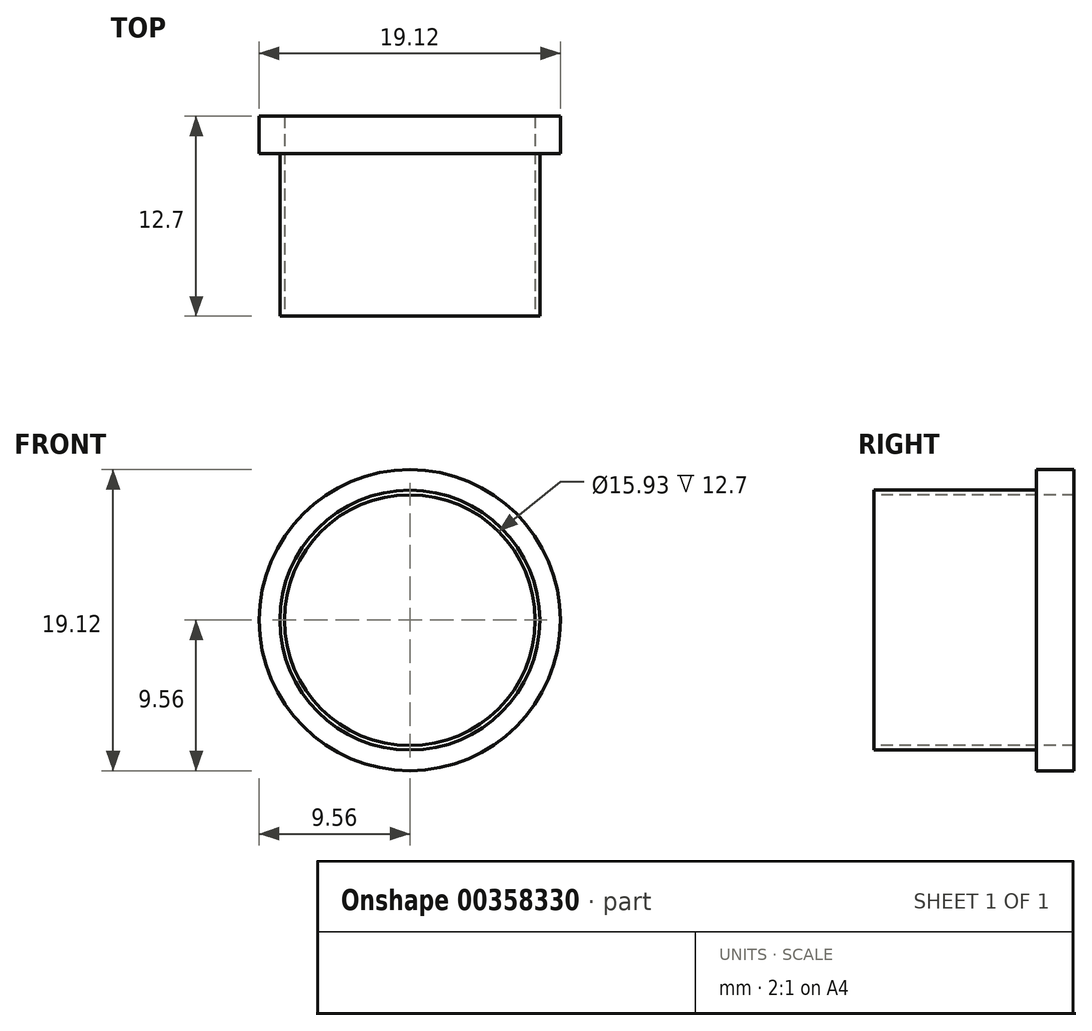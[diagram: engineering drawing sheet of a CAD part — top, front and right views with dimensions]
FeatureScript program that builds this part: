
annotation { "Feature Type Name" : "Feature", "Feature Type Description" : "" }
export const myFeature = defineFeature(function(context is Context, id is Id, definition is map)
    precondition{}
    {
        {
            var Q0;
            Q0=qCreatedBy(makeId("Front.planeOp"),FACE);
            var sketch = newSketch(context, id + "F0", { "sketchPlane" : qUnion([Q0])});
            skCircle(sketch, "E0", {"center": v(0, 0) * mm, "radius": 9.56 * mm});
            skSolve(sketch);
        }
        {
            var Q0;
            Q0=makeQuery(id+"F0.imprint","IMPRINT",FACE,{"disambiguationData":[TD([[makeQuery(id+"F0.imprint","IMPRINT",EDGE,{"derivedFrom":sQuery(id+"F0.wireOp",EDGE,"E0")}),1.0]])]});
            extrude(context, id + "F1", {"entities" : qUnion([Q0]), "depth" : 2.4 * mm});
        }
        {
            var Q0;
            Q0=makeQuery(id+"F1.opExtrude","CAP_FACE",FACE,{"disambiguationData":[OSD([sQuery(id+"F0.wireOp",EDGE,"E0")])],"isStart":false});
            var sketch = newSketch(context, id + "F2", { "sketchPlane" : qUnion([Q0])});
            skCircle(sketch, "E1", {"center": v(0, 0) * mm, "radius": 8.26 * mm});
            skSolve(sketch);
        }
        {
            var Q0;
            Q0 = qSketchRegion(id + "F2", true);
            extrude(context, id + "F3", {"entities" : qUnion([Q0]), "operationType" : NewBodyOperationType.ADD, "depth" : 10.3 * mm});
        }
        {
            var Q0;
            Q0=makeQuery(id+"F3.opExtrude","CAP_FACE",FACE,{"disambiguationData":[OSD([sQuery(id+"F2.wireOp",EDGE,"E1")])],"isStart":false});
            var sketch = newSketch(context, id + "F4", { "sketchPlane" : qUnion([Q0])});
            skCircle(sketch, "E2", {"center": v(0, 0) * mm, "radius": 7.96 * mm});
            skSolve(sketch);
        }
        {
            var Q0;
            Q0 = qSketchRegion(id + "F4", true);
            extrude(context, id + "F5", {"entities" : qUnion([Q0]), "operationType" : NewBodyOperationType.REMOVE, "endBound" : BoundingType.THROUGH_ALL, "oppositeDirection" : true, "depth" : 25 * mm});
        }
    });
